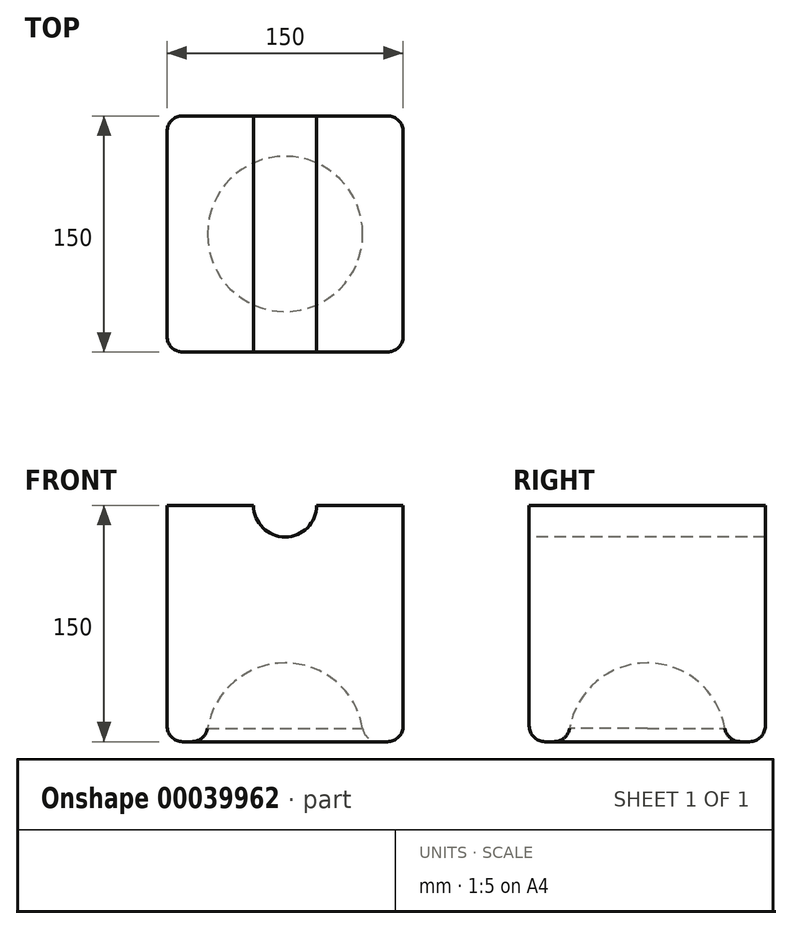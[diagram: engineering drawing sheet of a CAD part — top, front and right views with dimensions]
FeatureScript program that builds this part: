
annotation { "Feature Type Name" : "Feature", "Feature Type Description" : "" }
export const myFeature = defineFeature(function(context is Context, id is Id, definition is map)
    precondition{}
    {
        {
            var Q0;
            Q0=qCreatedBy(makeId("Front.planeOp"),FACE);
            var sketch = newSketch(context, id + "F0", { "sketchPlane" : qUnion([Q0])});
            skLineSegment(sketch, "E0.rect.bottom", {"start": v(-75, 75) * mm, "end": v(75, 75) * mm});
            skLineSegment(sketch, "E0.rect.top", {"start": v(-75, -75) * mm, "end": v(75, -75) * mm});
            skLineSegment(sketch, "E0.rect.left", {"start": v(-75, 75) * mm, "end": v(-75, -75) * mm});
            skLineSegment(sketch, "E0.rect.right", {"start": v(75, 75) * mm, "end": v(75, -75) * mm});
            skPoint(sketch, "E0.rect.middle", {"position": v(0, 0) * mm});
            skSolve(sketch);
        }
        {
            var Q0;
            Q0 = qSketchRegion(id + "F0", true);
            extrude(context, id + "F1", {"entities" : qUnion([Q0]), "endBound" : BoundingType.SYMMETRIC, "depth" : 150 * mm});
        }
        {
            var Q0;
            Q0=makeQuery(id+"F1.opExtrude","SWEPT_FACE",FACE,{"disambiguationData":[OSD([sQuery(id+"F0.wireOp",EDGE,"E0.rect.top")])]});
            var sketch = newSketch(context, id + "F2", { "sketchPlane" : qUnion([Q0])});
            skArc(sketch, "E1", {"start": v(-50, 0) * mm, "mid": v(0, -50) * mm, "end": v(50, 0) * mm});
            skLineSegment(sketch, "E2", {"start": v(-50, 0) * mm, "end": v(50, 0) * mm});
            skPoint(sketch, "E3.orphan", {"position": v(-71.71, 0) * mm});
            skSolve(sketch);
        }
        {
            var Q0;
            Q0=makeQuery(id+"F2.imprint","IMPRINT",FACE,{"disambiguationData":[TD([[makeQuery(id+"F2.imprint","IMPRINT",EDGE,{"derivedFrom":sQuery(id+"F2.wireOp",EDGE,"E1")}),-1.0]])]});
            var sketch = newSketch(context, id + "F3", { "sketchPlane" : qUnion([Q0])});
            skLineSegment(sketch, "E4", {"start": v(-100.5, 0) * mm, "end": v(112.58, 0) * mm, "construction": true});
            skSolve(sketch);
        }
        {
            var Q0;
            Q0 = qSketchRegion(id + "F2", true);
            var Q1;
            Q1=sQuery(id+"F3.wireOp",EDGE,"E4");
            revolve(context, id + "F4", {"operationType" : NewBodyOperationType.REMOVE, "entities" : qUnion([Q0]), "axis" : qUnion([Q1]), "revolveType" : RevolveType.FULL, "oppositeDirection" : true});
        }
        {
            var Q0;
            Q0=makeQuery(id+"F1.opExtrude","CAP_EDGE",EDGE,{"disambiguationData":[OSD([sQuery(id+"F0.wireOp",EDGE,"E0.rect.top")])],"isStart":true});
            var Q1;
            Q1=makeQuery(id+"F1.opExtrude","SWEPT_EDGE",EDGE,{"disambiguationData":[OSD([sQuery(id+"F0.wireOp",EDGE,"E0.rect.top"),sQuery(id+"F0.wireOp",EDGE,"E0.rect.right")])]});
            var Q2;
            Q2=makeQuery(id+"F1.opExtrude","CAP_EDGE",EDGE,{"disambiguationData":[OSD([sQuery(id+"F0.wireOp",EDGE,"E0.rect.top")])],"isStart":false});
            var Q3;
            Q3=makeQuery(id+"F1.opExtrude","SWEPT_EDGE",EDGE,{"disambiguationData":[OSD([sQuery(id+"F0.wireOp",EDGE,"E0.rect.top"),sQuery(id+"F0.wireOp",EDGE,"E0.rect.left")])]});
            var Q4;
            Q4=makeQuery(id+"F1.opExtrude","CAP_EDGE",EDGE,{"disambiguationData":[OSD([sQuery(id+"F0.wireOp",EDGE,"E0.rect.left")])],"isStart":false});
            var Q5;
            Q5=makeQuery(id+"F1.opExtrude","CAP_EDGE",EDGE,{"disambiguationData":[OSD([sQuery(id+"F0.wireOp",EDGE,"E0.rect.left")])],"isStart":true});
            var Q6;
            Q6=makeQuery(id+"F1.opExtrude","CAP_EDGE",EDGE,{"disambiguationData":[OSD([sQuery(id+"F0.wireOp",EDGE,"E0.rect.right")])],"isStart":true});
            var Q7;
            Q7=makeQuery(id+"F1.opExtrude","CAP_EDGE",EDGE,{"disambiguationData":[OSD([sQuery(id+"F0.wireOp",EDGE,"E0.rect.right")])],"isStart":false});
            var Q8;
            Q8=makeQuery(id+"F4.boolean.opBoolean","INTERSECT",EDGE,{"derivedFrom":[makeQuery(id+"F1.opExtrude","SWEPT_FACE",FACE,{"disambiguationData":[OSD([sQuery(id+"F0.wireOp",EDGE,"E0.rect.top")])]}),makeQuery(id+"F4.opRevolve","SWEPT_FACE",FACE,{"disambiguationData":[OSD([sQuery(id+"F2.wireOp",EDGE,"E1")])]})]});
            fillet(context, id + "F5", {"entities" : qUnion([Q0, Q1, Q2, Q3, Q4, Q5, Q6, Q7, Q8]), "radius" : 10 * mm, "tangentPropagation" : true, "allowEdgeOverflow" : false});
        }
        {
            var Q0;
            Q0=makeQuery(id+"F1.opExtrude","CAP_FACE",FACE,{"disambiguationData":[OSD([sQuery(id+"F0.wireOp",EDGE,"E0.rect.bottom"),sQuery(id+"F0.wireOp",EDGE,"E0.rect.top"),sQuery(id+"F0.wireOp",EDGE,"E0.rect.left"),sQuery(id+"F0.wireOp",EDGE,"E0.rect.right")])],"isStart":false});
            var sketch = newSketch(context, id + "F6", { "sketchPlane" : qUnion([Q0])});
            skArc(sketch, "E5", {"start": v(-20, 75) * mm, "mid": v(0, 55) * mm, "end": v(20, 75) * mm});
            skLineSegment(sketch, "E6", {"start": v(-20, 75) * mm, "end": v(20, 75) * mm});
            skSolve(sketch);
        }
        {
            var Q0;
            Q0 = qSketchRegion(id + "F6", true);
            extrude(context, id + "F7", {"entities" : qUnion([Q0]), "operationType" : NewBodyOperationType.REMOVE, "endBound" : BoundingType.UP_TO_NEXT, "oppositeDirection" : true, "depth" : 166 * mm});
        }
    });
